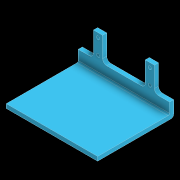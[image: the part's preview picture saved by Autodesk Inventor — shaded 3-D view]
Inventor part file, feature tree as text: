
AUTODESK INVENTOR PART (.ipt)
format: ipt  version: 2020 (Build 240168000, 168)  size: 180,224 bytes
history: native  units: mm
features: extrude x5, sketch x5, other x4, fillet x3
ambient origin geometry x8: Origin, YZ Plane, XZ Plane, XY Plane, X Axis, Y Axis, Z Axis, Center Point
bodies: Body1 (feature_tree)
feature tree (17):
  other  "實體1"
  extrude  "擠出1"  Depth=33.0mm
  extrude  "擠出2"  Depth=33.0mm
  extrude  "擠出3"  Depth=220.0mm
  extrude  "擠出4"  Depth=110.0mm
  extrude  "擠出5"  Depth=88.0mm
  fillet  "圓角1"  Radius=88.0mm
  fillet  "圓角2"  Radius=55.0mm
  fillet  "圓角3"  Radius=55.0mm
  sketch  "草圖1"
  sketch  "草圖2"
  sketch  "草圖3"
  sketch  "草圖4"
  sketch  "草圖5"
  other  "投影切割邊1"
  other  "投影切割邊2"
  other  "投影切割邊3"
